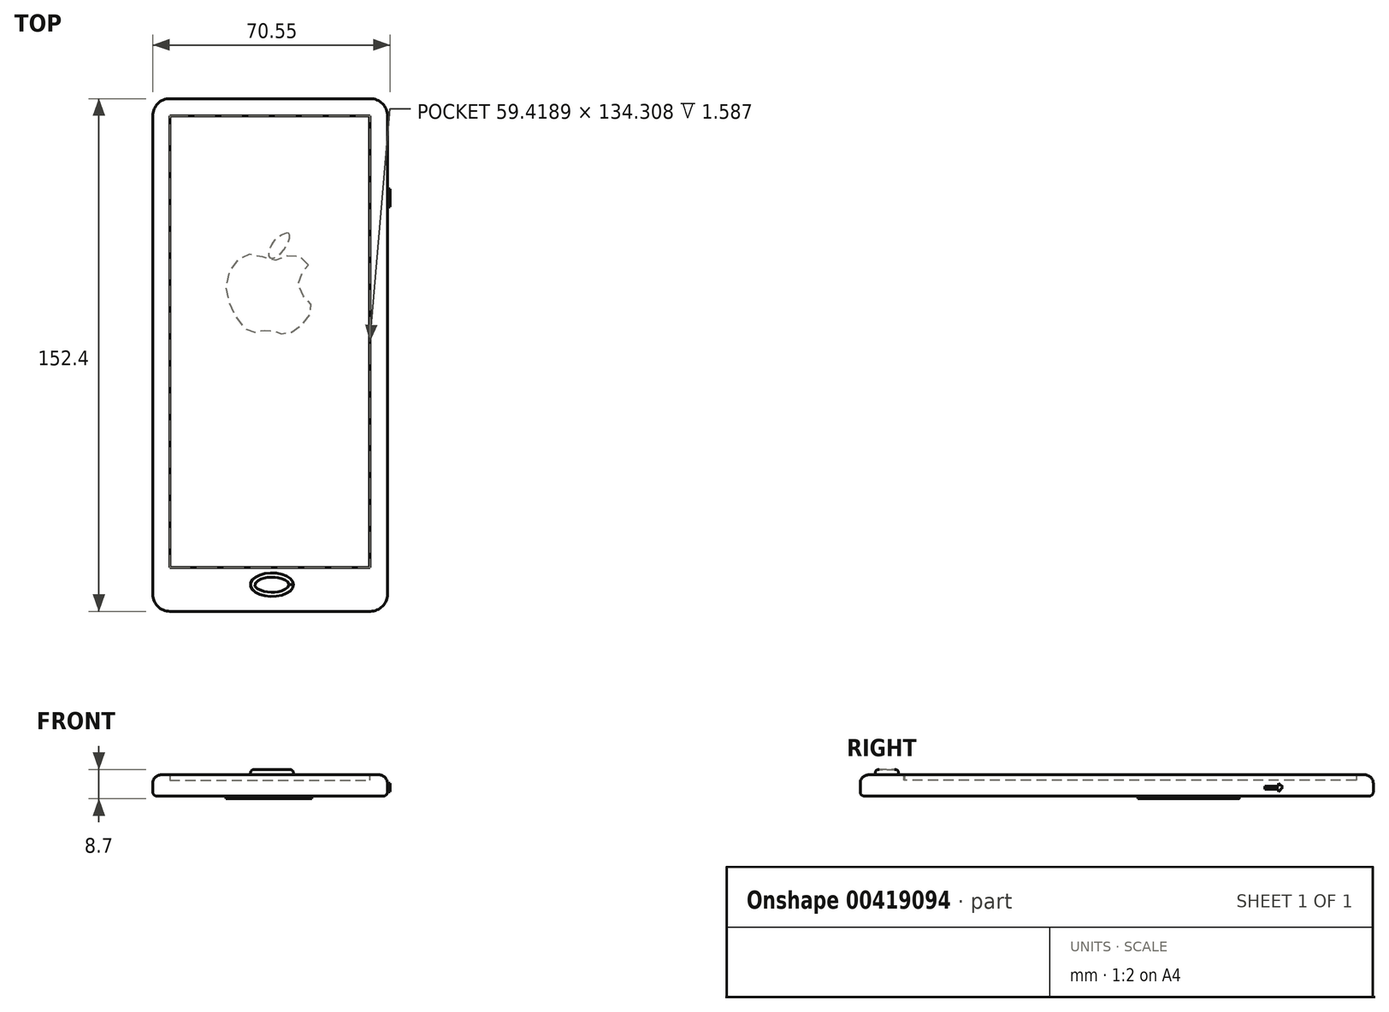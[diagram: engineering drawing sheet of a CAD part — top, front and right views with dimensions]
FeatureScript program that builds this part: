
annotation { "Feature Type Name" : "Feature", "Feature Type Description" : "" }
export const myFeature = defineFeature(function(context is Context, id is Id, definition is map)
    precondition{}
    {
        {
            var Q0;
            Q0=qCreatedBy(makeId("Top.planeOp"),FACE);
            var sketch = newSketch(context, id + "F0", { "sketchPlane" : qUnion([Q0])});
            skLineSegment(sketch, "E0.bottom", {"start": v(-43.97, 95.55) * mm, "end": v(25.76, 95.55) * mm});
            skLineSegment(sketch, "E0.top", {"start": v(-43.97, -56.85) * mm, "end": v(25.76, -56.85) * mm});
            skLineSegment(sketch, "E0.left", {"start": v(-43.97, 95.55) * mm, "end": v(-43.97, -56.85) * mm});
            skLineSegment(sketch, "E0.right", {"start": v(25.76, 95.55) * mm, "end": v(25.76, -56.85) * mm});
            skSolve(sketch);
        }
        {
            var Q0;
            Q0=makeQuery(id+"F0.imprint","IMPRINT",FACE,{"disambiguationData":[TD([[makeQuery(id+"F0.imprint","IMPRINT",EDGE,{"derivedFrom":sQuery(id+"F0.wireOp",EDGE,"E0.bottom")}),-1.0]])]});
            extrude(context, id + "F1", {"entities" : qUnion([Q0]), "depth" : 6.35 * mm});
        }
        {
            var Q0;
            Q0=makeQuery(id+"F1.opExtrude","SWEPT_EDGE",EDGE,{"disambiguationData":[OSD([sQuery(id+"F0.wireOp",EDGE,"E0.bottom"),sQuery(id+"F0.wireOp",EDGE,"E0.right")])]});
            var Q1;
            Q1=makeQuery(id+"F1.opExtrude","SWEPT_EDGE",EDGE,{"disambiguationData":[OSD([sQuery(id+"F0.wireOp",EDGE,"E0.bottom"),sQuery(id+"F0.wireOp",EDGE,"E0.left")])]});
            var Q2;
            Q2=makeQuery(id+"F1.opExtrude","SWEPT_EDGE",EDGE,{"disambiguationData":[OSD([sQuery(id+"F0.wireOp",EDGE,"E0.top"),sQuery(id+"F0.wireOp",EDGE,"E0.right")])]});
            var Q3;
            Q3=makeQuery(id+"F1.opExtrude","SWEPT_EDGE",EDGE,{"disambiguationData":[OSD([sQuery(id+"F0.wireOp",EDGE,"E0.top"),sQuery(id+"F0.wireOp",EDGE,"E0.left")])]});
            fillet(context, id + "F2", {"entities" : qUnion([Q0, Q1, Q2, Q3]), "radius" : 5.08 * mm, "tangentPropagation" : true, "allowEdgeOverflow" : false});
        }
        {
            var Q0;
            Q0=makeQuery(id+"F1.opExtrude","CAP_FACE",FACE,{"disambiguationData":[OSD([sQuery(id+"F0.wireOp",EDGE,"E0.bottom"),sQuery(id+"F0.wireOp",EDGE,"E0.top"),sQuery(id+"F0.wireOp",EDGE,"E0.left"),sQuery(id+"F0.wireOp",EDGE,"E0.right")])],"isStart":false});
            var sketch = newSketch(context, id + "F3", { "sketchPlane" : qUnion([Q0])});
            skLineSegment(sketch, "E1.bottom", {"start": v(-38.9, 90.47) * mm, "end": v(20.53, 90.47) * mm});
            skLineSegment(sketch, "E1.top", {"start": v(-38.9, -43.84) * mm, "end": v(20.53, -43.84) * mm});
            skLineSegment(sketch, "E1.left", {"start": v(-38.9, 90.47) * mm, "end": v(-38.9, -43.84) * mm});
            skLineSegment(sketch, "E1.right", {"start": v(20.53, 90.47) * mm, "end": v(20.53, -43.84) * mm});
            skSolve(sketch);
        }
        {
            var Q0;
            Q0 = qSketchRegion(id + "F3", true);
            extrude(context, id + "F4", {"entities" : qUnion([Q0]), "operationType" : NewBodyOperationType.REMOVE, "oppositeDirection" : true, "depth" : 1.59 * mm});
        }
        {
            var Q0;
            Q0=makeQuery(id+"F1.opExtrude","CAP_EDGE",EDGE,{"disambiguationData":[OSD([sQuery(id+"F0.wireOp",EDGE,"E0.bottom")])],"isStart":false});
            fillet(context, id + "F5", {"entities" : qUnion([Q0]), "radius" : 2.54 * mm, "tangentPropagation" : true, "allowEdgeOverflow" : false});
        }
        {
            var Q0;
            Q0=makeQuery(id+"F1.opExtrude","CAP_FACE",FACE,{"disambiguationData":[OSD([sQuery(id+"F0.wireOp",EDGE,"E0.bottom"),sQuery(id+"F0.wireOp",EDGE,"E0.top"),sQuery(id+"F0.wireOp",EDGE,"E0.left"),sQuery(id+"F0.wireOp",EDGE,"E0.right")])],"isStart":false});
            var sketch = newSketch(context, id + "F6", { "sketchPlane" : qUnion([Q0])});
            skEllipse(sketch, "E2", {"center": v(-8.56, -48.92) * mm, "majorRadius": 6.4 * mm, "minorRadius": 3.5 * mm, "majorAxis": v(1, 0)});
            skSolve(sketch);
        }
        {
            var Q0;
            Q0=makeQuery(id+"F6.imprint","IMPRINT",FACE,{"disambiguationData":[TD([[makeQuery(id+"F6.imprint","IMPRINT",EDGE,{"derivedFrom":sQuery(id+"F6.wireOp",EDGE,"E2")}),1.0]])]});
            extrude(context, id + "F7", {"entities" : qUnion([Q0]), "depth" : 1.59 * mm});
        }
        {
            var Q0;
            Q0=makeQuery(id+"F7.opExtrude","CAP_EDGE",EDGE,{"disambiguationData":[OSD([sQuery(id+"F6.wireOp",EDGE,"E2")])],"isStart":false});
            fillet(context, id + "F8", {"entities" : qUnion([Q0]), "radius" : 1.27 * mm, "rho" : 0.5, "crossSection" : FilletCrossSection.CONIC, "allowEdgeOverflow" : false});
        }
        {
            var Q0;
            Q0=makeQuery(id+"F1.opExtrude","CAP_EDGE",EDGE,{"disambiguationData":[OSD([sQuery(id+"F0.wireOp",EDGE,"E0.left")])],"isStart":true});
            fillet(context, id + "F9", {"entities" : qUnion([Q0]), "radius" : 1.27 * mm, "tangentPropagation" : true, "allowEdgeOverflow" : false});
        }
        {
            var Q0;
            Q0=makeQuery(id+"F1.opExtrude","SWEPT_FACE",FACE,{"disambiguationData":[OSD([sQuery(id+"F0.wireOp",EDGE,"E0.right")])]});
            var sketch = newSketch(context, id + "F10", { "sketchPlane" : qUnion([Q0])});
            skLineSegment(sketch, "E3", {"start": v(63.32, 2.85) * mm, "end": v(63.32, 2.02) * mm});
            skLineSegment(sketch, "E4", {"start": v(63.32, 2.02) * mm, "end": v(67.4, 2.02) * mm});
            skLineSegment(sketch, "E5", {"start": v(67.4, 2.02) * mm, "end": v(67.4, 1.27) * mm});
            skLineSegment(sketch, "E6", {"start": v(67.4, 1.27) * mm, "end": v(68.7, 2.72) * mm});
            skLineSegment(sketch, "E7", {"start": v(68.7, 2.72) * mm, "end": v(67.4, 3.81) * mm});
            skLineSegment(sketch, "E8", {"start": v(67.4, 3.81) * mm, "end": v(67.4, 3) * mm});
            skLineSegment(sketch, "E9", {"start": v(67.4, 3) * mm, "end": v(63.32, 3) * mm});
            skLineSegment(sketch, "E10", {"start": v(63.32, 3) * mm, "end": v(63.32, 2.85) * mm});
            skSolve(sketch);
        }
        {
            var Q0;
            Q0=makeQuery(id+"F10.imprint","IMPRINT",FACE,{"disambiguationData":[TD([[makeQuery(id+"F10.imprint","IMPRINT",EDGE,{"derivedFrom":sQuery(id+"F10.wireOp",EDGE,"E3")}),1.0]])]});
            extrude(context, id + "F11", {"entities" : qUnion([Q0]), "depth" : 0.83 * mm});
        }
        {
            var Q0;
            Q0=makeQuery(id+"F4.boolean.opBoolean","COPY",FACE,{"derivedFrom":makeQuery(id+"F4.opExtrude","CAP_FACE",FACE,{"disambiguationData":[OSD([sQuery(id+"F3.wireOp",EDGE,"E1.bottom"),sQuery(id+"F3.wireOp",EDGE,"E1.top"),sQuery(id+"F3.wireOp",EDGE,"E1.left"),sQuery(id+"F3.wireOp",EDGE,"E1.right")])],"isStart":false})});
            var sketch = newSketch(context, id + "F12", { "sketchPlane" : qUnion([Q0])});
            skLineSegment(sketch, "E11.bottom", {"start": v(-38.96, 90.55) * mm, "end": v(20.45, 90.55) * mm});
            skLineSegment(sketch, "E11.top", {"start": v(-38.96, -43.75) * mm, "end": v(20.45, -43.75) * mm});
            skLineSegment(sketch, "E11.left", {"start": v(-38.96, 90.55) * mm, "end": v(-38.96, -43.75) * mm});
            skLineSegment(sketch, "E11.right", {"start": v(20.45, 90.55) * mm, "end": v(20.45, -43.75) * mm});
            skSolve(sketch);
        }
        {
            var Q0;
            {var subQ0=sQuery(id+"F12.wireOp",EDGE,"E11.right");var subQ1=sQuery(id+"F12.wireOp",EDGE,"E11.top");var subQ2=makeQuery(id+"F12.imprint","INTERSECT",VERTEX,{"derivedFrom":[subQ1,subQ0]});Q0=makeQuery(id+"F12.imprint","IMPRINT",FACE,{"disambiguationData":[TD([[makeQuery(id+"F12.imprint","IMPRINT",EDGE,{"disambiguationData":[TD([[subQ2,1.0]])],"derivedFrom":subQ1}),1.0]])]});}
            extrude(context, id + "F13", {"entities" : qUnion([Q0]), "depth" : 1.59 * mm});
        }
        {
            var Q0;
            Q0=makeQuery(id+"F1.opExtrude","CAP_FACE",FACE,{"disambiguationData":[OSD([sQuery(id+"F0.wireOp",EDGE,"E0.bottom"),sQuery(id+"F0.wireOp",EDGE,"E0.top"),sQuery(id+"F0.wireOp",EDGE,"E0.left"),sQuery(id+"F0.wireOp",EDGE,"E0.right")])],"isStart":true});
            var sketch = newSketch(context, id + "F14", { "sketchPlane" : qUnion([Q0])});
            skFitSpline(sketch, "E12", {"points": [v(2.27, -46.11) * mm, v(-2.19, -49.18) * mm, v(-7.49, -47.5) * mm, v(-13.62, -49.18) * mm, v(-19.2, -47.23) * mm, v(-22.26, -39.98) * mm, v(-19.75, -31.61) * mm, v(-15.3, -26.32) * mm, v(-11.39, -26.6) * mm, v(-8.32, -26.6) * mm, v(-6.1, -25.76) * mm, v(-2.47, -26.32) * mm, v(2.27, -30.5) * mm, v(3.1, -34.12) * mm, v(0, -38.03) * mm, v(0, -43.32) * mm, v(2.27, -46.11) * mm]});
            skFitSpline(sketch, "E13", {"points": [v(-3.51, -55.54) * mm, v(-6.87, -54.17) * mm, v(-8.85, -51.81) * mm, v(-9.33, -48.35) * mm, v(-5.54, -49.97) * mm, v(-3.51, -55.54) * mm]});
            skSolve(sketch);
        }
        {
            var Q0;
            Q0 = qSketchRegion(id + "F14", true);
            extrude(context, id + "F15", {"entities" : qUnion([Q0]), "depth" : 0.76 * mm});
        }
    });
